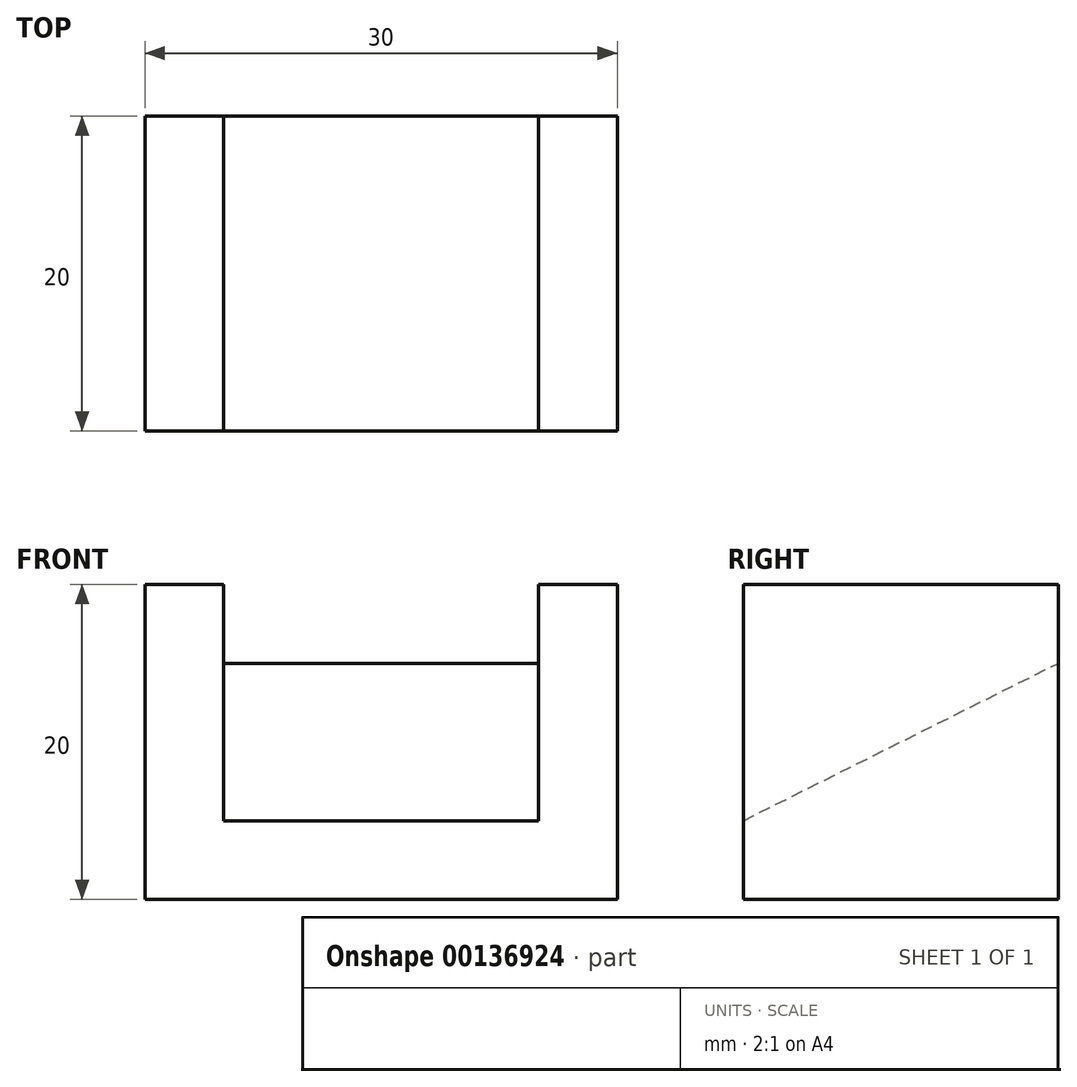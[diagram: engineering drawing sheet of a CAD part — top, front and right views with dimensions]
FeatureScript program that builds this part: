
annotation { "Feature Type Name" : "Feature", "Feature Type Description" : "" }
export const myFeature = defineFeature(function(context is Context, id is Id, definition is map)
    precondition{}
    {
        {
            var Q0;
            Q0=qCreatedBy(makeId("Front.planeOp"),FACE);
            var sketch = newSketch(context, id + "F0", { "sketchPlane" : qUnion([Q0])});
            skLineSegment(sketch, "E0", {"start": v(15, 0) * mm, "end": v(-15, 0) * mm});
            skLineSegment(sketch, "E1", {"start": v(-15, 0) * mm, "end": v(-15, 20) * mm});
            skLineSegment(sketch, "E2", {"start": v(-15, 20) * mm, "end": v(15, 20) * mm});
            skLineSegment(sketch, "E3", {"start": v(15, 20) * mm, "end": v(15, 0) * mm});
            skSolve(sketch);
        }
        {
            var Q0;
            Q0 = qSketchRegion(id + "F0", true);
            extrude(context, id + "F1", {"entities" : qUnion([Q0]), "oppositeDirection" : true, "depth" : 20 * mm});
        }
        {
            var Q0;
            Q0=qCreatedBy(makeId("Right.planeOp"),FACE);
            var sketch = newSketch(context, id + "F2", { "sketchPlane" : qUnion([Q0])});
            skLineSegment(sketch, "E4", {"start": v(0, 5) * mm, "end": v(20, 15) * mm});
            skLineSegment(sketch, "E5", {"start": v(20, 15) * mm, "end": v(20, 20) * mm});
            skLineSegment(sketch, "E6", {"start": v(20, 20) * mm, "end": v(0, 20) * mm});
            skLineSegment(sketch, "E7", {"start": v(0, 20) * mm, "end": v(0, 5) * mm});
            skSolve(sketch);
        }
        {
            var Q0;
            Q0 = qSketchRegion(id + "F2", true);
            extrude(context, id + "F3", {"entities" : qUnion([Q0]), "operationType" : NewBodyOperationType.REMOVE, "endBound" : BoundingType.SYMMETRIC, "oppositeDirection" : true, "depth" : 20 * mm});
        }
    });
